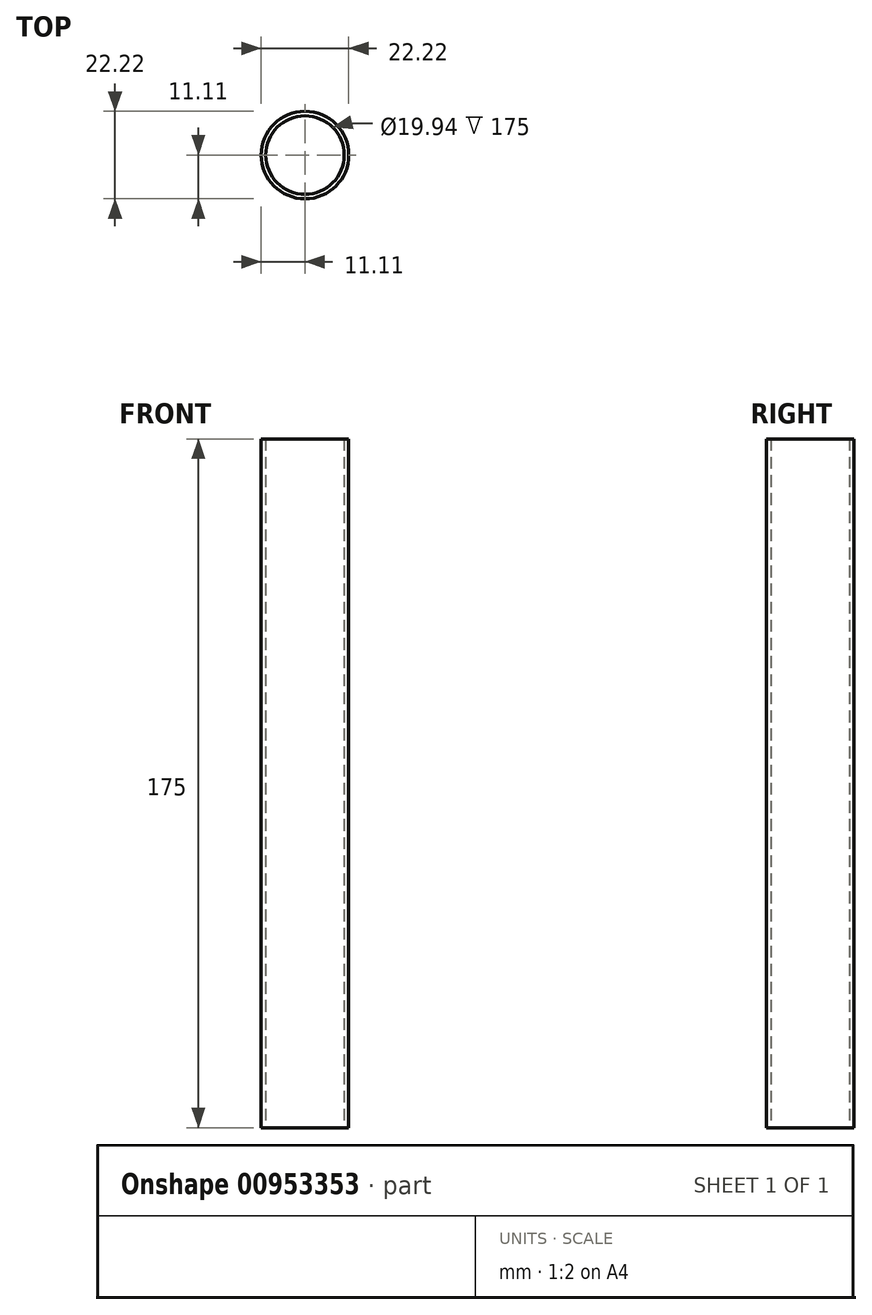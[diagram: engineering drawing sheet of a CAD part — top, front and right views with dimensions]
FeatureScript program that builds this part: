
annotation { "Feature Type Name" : "Feature", "Feature Type Description" : "" }
export const myFeature = defineFeature(function(context is Context, id is Id, definition is map)
    precondition{}
    {
        {
            var Q0;
            Q0=qCreatedBy(makeId("Top.planeOp"),FACE);
            var sketch = newSketch(context, id + "F0", { "sketchPlane" : qUnion([Q0])});
            skCircle(sketch, "E0", {"center": v(0, 0) * mm, "radius": 11.11 * mm});
            skCircle(sketch, "E1.0", {"center": v(0, 0) * mm, "radius": 9.97 * mm});
            skSolve(sketch);
        }
        {
            var Q0;
            Q0=qSketchRegion(id+"F0",true);
            extrude(context, id + "F1", {"entities" : qUnion([Q0]), "depth" : 175 * mm, "offsetDistance" : 25 * mm});
        }
    });
